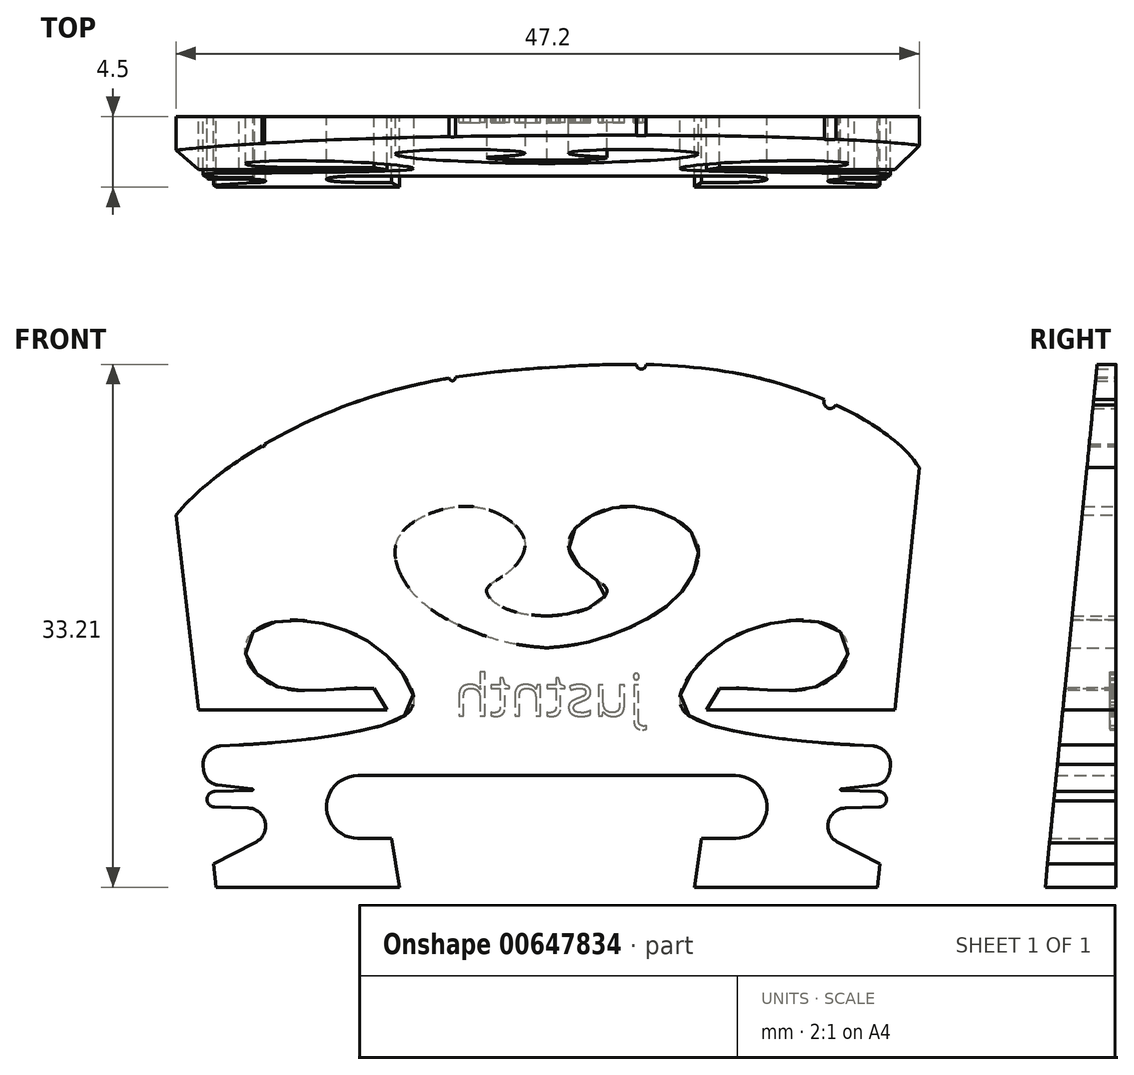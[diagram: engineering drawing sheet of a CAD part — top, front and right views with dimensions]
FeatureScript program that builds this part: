
annotation { "Feature Type Name" : "Feature", "Feature Type Description" : "" }
export const myFeature = defineFeature(function(context is Context, id is Id, definition is map)
    precondition{}
    {
        {
            var Q0;
            Q0=qCreatedBy(makeId("Front.planeOp"),FACE);
            var sketch = newSketch(context, id + "F0", { "sketchPlane" : qUnion([Q0])});
            skFitSpline(sketch, "E0", {"points": [v(-23.54, 23.66) * mm, v(-12.1, 30.83) * mm, v(0, 33) * mm, v(13.95, 32.22) * mm, v(23.66, 26.65) * mm], "startDerivative": vector(29.69, 35.16) * mm, "endDerivative": vector(19.16, -29.67) * mm});
            skLineSegment(sketch, "E1", {"start": v(9.82, 3.09) * mm, "end": v(12, 3.1) * mm});
            skLineSegment(sketch, "E2", {"start": v(12, 7.1) * mm, "end": v(0, 7.1) * mm});
            skArc(sketch, "E3.filletArc", {"start": v(12, 3.1) * mm, "mid": v(14, 5.1) * mm, "end": v(12, 7.1) * mm});
            skLineSegment(sketch, "E4", {"start": v(21, 0) * mm, "end": v(21.16, 1.5) * mm});
            skPoint(sketch, "E5.visualSharp", {"position": v(11.23, 5.08) * mm});
            skFitSpline(sketch, "E6", {"points": [v(0, 15.2) * mm, v(4, 15.99) * mm, v(8.17, 18.33) * mm, v(9.57, 21.81) * mm, v(7.19, 23.82) * mm, v(3.6, 23.93) * mm, v(1.4, 21.97) * mm, v(2.5, 19.96) * mm, v(3.82, 18.86) * mm, v(2.74, 17.76) * mm, v(0, 17.22) * mm], "startDerivative": vector(53.54, 4.7) * mm, "endDerivative": vector(-27.32, -1.62) * mm});
            skFitSpline(sketch, "E7.MirrorCS", {"points": [v(0, 15.2) * mm, v(-4, 15.99) * mm, v(-8.17, 18.33) * mm, v(-9.57, 21.81) * mm, v(-7.19, 23.82) * mm, v(-3.6, 23.93) * mm, v(-1.4, 21.97) * mm, v(-2.5, 19.96) * mm, v(-3.82, 18.86) * mm, v(-2.74, 17.76) * mm, v(0, 17.22) * mm], "startDerivative": vector(-53.54, 4.7) * mm, "endDerivative": vector(27.32, -1.62) * mm});
            skLineSegment(sketch, "E8.MirrorCS", {"start": v(-12, 7.1) * mm, "end": v(0, 7.1) * mm});
            skArc(sketch, "E9.MirrorCS", {"start": v(-12.01, 3.1) * mm, "mid": v(-14, 5.1) * mm, "end": v(-12, 7.1) * mm});
            skLineSegment(sketch, "E10.MirrorCS", {"start": v(-9.85, 3.08) * mm, "end": v(-12.01, 3.1) * mm});
            skLineSegment(sketch, "E11", {"start": v(-21.16, 1.5) * mm, "end": v(-21, 0) * mm});
            skFitSpline(sketch, "E12.MirrorCS", {"points": [v(10.96, 12.63) * mm, v(17.29, 12.8) * mm, v(19.14, 15.37) * mm, v(17, 16.9) * mm, v(12.21, 16.08) * mm, v(9.91, 14.46) * mm, v(8.57, 12.54) * mm, v(9.18, 10.8) * mm, v(19.55, 9.04) * mm], "startDerivative": vector(28.37, 3.52) * mm, "endDerivative": vector(23.7, -0.72) * mm});
            skLineSegment(sketch, "E13.MirrorCS", {"start": v(10.96, 12.63) * mm, "end": v(10.14, 11.25) * mm});
            skLineSegment(sketch, "E14", {"start": v(-18, 62.47) * mm, "end": v(-18, 22.93) * mm, "construction": true});
            skLineSegment(sketch, "E15", {"start": v(6, 60.56) * mm, "end": v(6, 29.37) * mm, "construction": true});
            skLineSegment(sketch, "E16", {"start": v(18, 61.03) * mm, "end": v(18, 25.82) * mm, "construction": true});
            skLineSegment(sketch, "E17", {"start": v(-6, 62.47) * mm, "end": v(-6, 28.49) * mm, "construction": true});
            skCircle(sketch, "E18", {"center": v(-18, 28.08) * mm, "radius": 0.1 * mm});
            skCircle(sketch, "E19", {"center": v(-6, 32.36) * mm, "radius": 0.2 * mm});
            skCircle(sketch, "E20", {"center": v(18, 30.8) * mm, "radius": 0.4 * mm});
            skCircle(sketch, "E21", {"center": v(6, 33.2) * mm, "radius": 0.3 * mm});
            skLineSegment(sketch, "E22", {"start": v(23.66, 26.65) * mm, "end": v(22.12, 11.25) * mm});
            skLineSegment(sketch, "E23", {"start": v(22.12, 11.25) * mm, "end": v(10.14, 11.25) * mm});
            skLineSegment(sketch, "E24", {"start": v(21.16, 1.5) * mm, "end": v(18.56, 2.82) * mm});
            skLineSegment(sketch, "E25", {"start": v(20.7, 8.97) * mm, "end": v(19.55, 9.04) * mm});
            skLineSegment(sketch, "E26", {"start": v(18.96, 5.03) * mm, "end": v(21.1, 5.08) * mm});
            skArc(sketch, "E27", {"start": v(18.96, 5.03) * mm, "mid": v(17.86, 4.1) * mm, "end": v(18.56, 2.82) * mm});
            skPoint(sketch, "E28.visualSharp", {"position": v(21.52, 5.1) * mm});
            skArc(sketch, "E28.filletArc", {"start": v(21.1, 5.08) * mm, "mid": v(21.4, 5.2) * mm, "end": v(21.57, 5.47) * mm});
            skLineSegment(sketch, "E29", {"start": v(21.57, 5.47) * mm, "end": v(21.58, 5.52) * mm});
            skArc(sketch, "E30.filletArc", {"start": v(21.58, 5.52) * mm, "mid": v(21.45, 5.9) * mm, "end": v(21.08, 6.07) * mm});
            skArc(sketch, "E31.filletArc", {"start": v(21.83, 7.8) * mm, "mid": v(21.5, 8.6) * mm, "end": v(20.7, 8.97) * mm});
            skLineSegment(sketch, "E32", {"start": v(21.08, 6.07) * mm, "end": v(18.71, 6.15) * mm});
            skFitSpline(sketch, "E33.MirrorCS", {"points": [v(-10.96, 12.63) * mm, v(-17.29, 12.8) * mm, v(-19.14, 15.37) * mm, v(-17, 16.9) * mm, v(-12.21, 16.08) * mm, v(-9.91, 14.46) * mm, v(-8.57, 12.54) * mm, v(-9.18, 10.8) * mm, v(-19.55, 9.04) * mm], "startDerivative": vector(-28.37, 3.52) * mm, "endDerivative": vector(-23.7, -0.72) * mm});
            skLineSegment(sketch, "E34.MirrorCS", {"start": v(-10.96, 12.63) * mm, "end": v(-10.14, 11.25) * mm});
            skLineSegment(sketch, "E35.MirrorCS", {"start": v(-22.12, 11.25) * mm, "end": v(-10.14, 11.25) * mm});
            skLineSegment(sketch, "E36.MirrorCS", {"start": v(-18.96, 5.03) * mm, "end": v(-21.1, 5.08) * mm});
            skArc(sketch, "E37.MirrorCS", {"start": v(-18.96, 5.03) * mm, "mid": v(-17.86, 4.1) * mm, "end": v(-18.56, 2.82) * mm});
            skLineSegment(sketch, "E38.MirrorCS", {"start": v(-21.16, 1.5) * mm, "end": v(-18.56, 2.82) * mm});
            skLineSegment(sketch, "E39", {"start": v(-22.12, 11.25) * mm, "end": v(-23.54, 23.66) * mm});
            skLineSegment(sketch, "E40", {"start": v(18.7, 6.25) * mm, "end": v(20.9, 6.49) * mm});
            skLineSegment(sketch, "E41", {"start": v(21.78, 7.37) * mm, "end": v(21.83, 7.8) * mm});
            skArc(sketch, "E42.filletArc", {"start": v(20.9, 6.49) * mm, "mid": v(21.5, 6.77) * mm, "end": v(21.78, 7.37) * mm});
            skPoint(sketch, "E43.visualSharp", {"position": v(18, 6.17) * mm});
            skArc(sketch, "E43.filletArc", {"start": v(18.7, 6.25) * mm, "mid": v(18.66, 6.2) * mm, "end": v(18.71, 6.15) * mm});
            skLineSegment(sketch, "E44.MirrorCS", {"start": v(-20.7, 8.97) * mm, "end": v(-19.55, 9.04) * mm});
            skArc(sketch, "E45.MirrorCS", {"start": v(-21.83, 7.8) * mm, "mid": v(-21.5, 8.6) * mm, "end": v(-20.7, 8.97) * mm});
            skLineSegment(sketch, "E46.MirrorCS", {"start": v(-21.78, 7.37) * mm, "end": v(-21.83, 7.8) * mm});
            skArc(sketch, "E47.MirrorCS", {"start": v(-20.9, 6.49) * mm, "mid": v(-21.5, 6.77) * mm, "end": v(-21.78, 7.37) * mm});
            skLineSegment(sketch, "E48.MirrorCS", {"start": v(-18.7, 6.25) * mm, "end": v(-20.9, 6.49) * mm});
            skArc(sketch, "E49.MirrorCS", {"start": v(-18.7, 6.25) * mm, "mid": v(-18.66, 6.2) * mm, "end": v(-18.71, 6.15) * mm});
            skLineSegment(sketch, "E50.MirrorCS", {"start": v(-21.08, 6.07) * mm, "end": v(-18.71, 6.15) * mm});
            skArc(sketch, "E51.MirrorCS", {"start": v(-21.58, 5.52) * mm, "mid": v(-21.45, 5.9) * mm, "end": v(-21.08, 6.07) * mm});
            skArc(sketch, "E52.MirrorCS", {"start": v(-21.1, 5.08) * mm, "mid": v(-21.4, 5.2) * mm, "end": v(-21.57, 5.47) * mm});
            skLineSegment(sketch, "E53.MirrorCS", {"start": v(-21.57, 5.47) * mm, "end": v(-21.58, 5.52) * mm});
            skLineSegment(sketch, "E54", {"start": v(-9.85, 3.08) * mm, "end": v(-9.36, 0) * mm});
            skLineSegment(sketch, "E55", {"start": v(-9.36, 0) * mm, "end": v(-21, 0) * mm});
            skLineSegment(sketch, "E56", {"start": v(9.39, 0) * mm, "end": v(21, 0) * mm});
            skLineSegment(sketch, "E57", {"start": v(9.82, 3.09) * mm, "end": v(9.39, 0) * mm});
            skSolve(sketch);
        }
        {
            var Q0;
            {var subQ1=sQuery(id+"F0.wireOp",EDGE,"E0");Q0=makeQuery(id+"F0.imprint","IMPRINT",FACE,{"disambiguationData":[TD([[makeQuery(id+"F0.imprint","IMPRINT",EDGE,{"derivedFrom":subQ1}),-1.0]])]});}
            extrude(context, id + "F1", {"entities" : qUnion([Q0]), "depth" : 4.5 * mm, "offsetDistance" : 25.4 * mm});
        }
        {
            var Q0;
            Q0=qCreatedBy(makeId("Right.planeOp"),FACE);
            var sketch = newSketch(context, id + "F2", { "sketchPlane" : qUnion([Q0])});
            skLineSegment(sketch, "E58", {"start": v(-1.2, 78.1) * mm, "end": v(-1.2, 1.9) * mm});
            skLineSegment(sketch, "E59", {"start": v(12.46, 33.21) * mm, "end": v(-25.03, 33.21) * mm});
            skLineSegment(sketch, "E60", {"start": v(-4.5, -2.46) * mm, "end": v(-4.5, 45.63) * mm});
            skLineSegment(sketch, "E61", {"start": v(-1.2, 33.21) * mm, "end": v(-4.5, 0) * mm});
            skLineSegment(sketch, "E62", {"start": v(-4.5, 0) * mm, "end": v(-9, 0) * mm});
            skLineSegment(sketch, "E63", {"start": v(-9, 0) * mm, "end": v(-7.85, 33.21) * mm});
            skLineSegment(sketch, "E64", {"start": v(-7.85, 33.21) * mm, "end": v(-1.2, 33.21) * mm});
            skLineSegment(sketch, "E65.top", {"start": v(-7.85, 40.77) * mm, "end": v(-1.2, 40.77) * mm});
            skLineSegment(sketch, "E65.left", {"start": v(-7.85, 33.21) * mm, "end": v(-7.85, 40.77) * mm});
            skLineSegment(sketch, "E65.right", {"start": v(-1.2, 33.21) * mm, "end": v(-1.2, 40.77) * mm});
            skSolve(sketch);
        }
        {
            var Q0;
            {var subQ0=sQuery(id+"F2.wireOp",EDGE,"E62");Q0=makeQuery(id+"F2.imprint","IMPRINT",FACE,{"disambiguationData":[TD([[makeQuery(id+"F2.imprint","IMPRINT",EDGE,{"derivedFrom":subQ0}),-1.0]])]});}
            var Q1;
            {var subQ0=sQuery(id+"F2.wireOp",EDGE,"E61");Q1=makeQuery(id+"F2.imprint","IMPRINT",FACE,{"disambiguationData":[TD([[makeQuery(id+"F2.imprint","IMPRINT",EDGE,{"derivedFrom":subQ0}),-1.0]])]});}
            var Q2;
            {var subQ5=sQuery(id+"F2.wireOp",EDGE,"E65.left");Q2=makeQuery(id+"F2.imprint","IMPRINT",FACE,{"disambiguationData":[TD([[makeQuery(id+"F2.imprint","IMPRINT",EDGE,{"derivedFrom":subQ5}),-1.0]])]});}
            var Q3;
            {var subQ5=sQuery(id+"F2.wireOp",EDGE,"E65.right");Q3=makeQuery(id+"F2.imprint","IMPRINT",FACE,{"disambiguationData":[TD([[makeQuery(id+"F2.imprint","IMPRINT",EDGE,{"derivedFrom":subQ5}),1.0]])]});}
            extrude(context, id + "F3", {"entities" : qUnion([Q0, Q1, Q2, Q3]), "operationType" : NewBodyOperationType.REMOVE, "endBound" : BoundingType.SYMMETRIC, "depth" : 60 * mm, "offsetDistance" : 25.4 * mm});
        }
        {
            var Q0;
            Q0=makeQuery(id+"F1.opExtrude","CAP_FACE",FACE,{"disambiguationData":[OSD([sQuery(id+"F0.wireOp",EDGE,"E0"),sQuery(id+"F0.wireOp",EDGE,"e4hmPngl-bTp4-2FKX-qq5L-C8yQQZpSV2t0"),sQuery(id+"F0.wireOp",EDGE,"m3C9ovOK-315E-PIzk-nrXY-3GBNYPGDzf1G"),sQuery(id+"F0.wireOp",EDGE,"E1"),sQuery(id+"F0.wireOp",EDGE,"E2"),sQuery(id+"F0.wireOp",EDGE,"E3.filletArc"),sQuery(id+"F0.wireOp",EDGE,"E4"),sQuery(id+"F0.wireOp",EDGE,"E6"),sQuery(id+"F0.wireOp",EDGE,"E7.MirrorCS"),sQuery(id+"F0.wireOp",EDGE,"E8.MirrorCS"),sQuery(id+"F0.wireOp",EDGE,"E9.MirrorCS"),sQuery(id+"F0.wireOp",EDGE,"E10.MirrorCS"),sQuery(id+"F0.wireOp",EDGE,"369ba2a7-3018-45a9-8760-523ebc0fda910.MirrorCS"),sQuery(id+"F0.wireOp",EDGE,"99c2ba22-9a41-4c2a-bd8a-ffb563d2db590.MirrorCS"),sQuery(id+"F0.wireOp",EDGE,"E11"),sQuery(id+"F0.wireOp",EDGE,"sNap6CoO-IBVS-i1IY-ntVr-FjdyHk4U1fLk"),sQuery(id+"F0.wireOp",EDGE,"Q49nbHIn-tZww-OQF0-PmV4-upVZ2FfT46EY"),sQuery(id+"F0.wireOp",EDGE,"cacc4af9-22af-473b-8ac6-10344cc65f12.filletArc"),sQuery(id+"F0.wireOp",EDGE,"b2179551-9911-4662-ab98-ed61c98f1fae0.MirrorCS"),sQuery(id+"F0.wireOp",EDGE,"WLDu3wvJ-hjGy-TZ6D-QxCG-5IQINUcYNDWe"),sQuery(id+"F0.wireOp",EDGE,"c432bdc4-3a2f-4fb0-98df-54dfc78423e7.filletArc"),sQuery(id+"F0.wireOp",EDGE,"686801cf-beb7-4a0b-9bdc-b307e84039be.filletArc"),sQuery(id+"F0.wireOp",EDGE,"xwyop2li-xI9W-UFQn-VAwa-afb1EGiimQMJ"),sQuery(id+"F0.wireOp",EDGE,"5a9beed9-85af-4595-b0f8-0b7d7c26e17c"),sQuery(id+"F0.wireOp",EDGE,"bzGZhi7p-2t2n-dACa-pQoM-uhUXtXE2D66O"),sQuery(id+"F0.wireOp",EDGE,"yywPAmDP-Yir0-P9Cb-WB6Q-Zl7V1TjRpGde"),sQuery(id+"F0.wireOp",EDGE,"E12.MirrorCS"),sQuery(id+"F0.wireOp",EDGE,"E13.MirrorCS"),sQuery(id+"F0.wireOp",EDGE,"PqBrF7gv-Diou-TzOB-6hR5-WF0VOCTdd9Ml"),sQuery(id+"F0.wireOp",EDGE,"irIPY5CA-CWUD-HGs8-Lafv-b9PyqiYwdKW4"),sQuery(id+"F0.wireOp",EDGE,"N699qDvk-ju4z-pMcA-En7K-C2CTM2OkSit7"),sQuery(id+"F0.wireOp",EDGE,"uBNGByd7-gyzj-997R-8Wxi-t9WqYOMEbmyB"),sQuery(id+"F0.wireOp",EDGE,"5093e992-0bc9-46ed-b494-589bb84dc8b9.filletArc"),sQuery(id+"F0.wireOp",EDGE,"d6a4b0fc-a71b-4a5d-b080-7cea932b6cd3.filletArc"),sQuery(id+"F0.wireOp",EDGE,"E18"),sQuery(id+"F0.wireOp",EDGE,"E19"),sQuery(id+"F0.wireOp",EDGE,"E20"),sQuery(id+"F0.wireOp",EDGE,"E21"),sQuery(id+"F0.wireOp",EDGE,"zmxQx3sE-Abgh-AzOG-xcvg-COG9eKqwMoW1"),sQuery(id+"F0.wireOp",EDGE,"6rnEQyg1-XuVb-NNO3-yQ0c-2cqNmvtJoFj3"),sQuery(id+"F0.wireOp",EDGE,"a740fce4-74ea-4a46-8614-070f5a65ce19.filletArc"),sQuery(id+"F0.wireOp",EDGE,"47d1662d-1cdc-404f-a2f1-9a71518fff21.filletArc"),sQuery(id+"F0.wireOp",EDGE,"x81WzDIV-gmfL-YwrE-CoO7-FSQeT6FRB7PQ"),sQuery(id+"F0.wireOp",EDGE,"GdfCoyAb-hPPH-aXcI-0p9N-VLlFjwOMujNR"),sQuery(id+"F0.wireOp",EDGE,"af57f127-2944-47e9-8a9b-73b34502bf92.filletArc"),sQuery(id+"F0.wireOp",EDGE,"19e7adce-8ca8-4fdb-b1fc-b8dd92e8bc45.filletArc")])],"isStart":true});
            var sketch = newSketch(context, id + "F4", { "sketchPlane" : qUnion([Q0])});
            skText(sketch, "E66", { "text": "justnth", "fontName": "OpenSans-Regular.ttf"});
            const initialGuessF4  = {"E66": [-0.00615, 0.01088, 1, 0, 0.00264]};
            skSetInitialGuess(sketch, initialGuessF4);
            skSolve(sketch);
        }
        {
            var Q0;
            Q0=qSketchRegion(id+"F4",true);
            extrude(context, id + "F5", {"entities" : qUnion([Q0]), "operationType" : NewBodyOperationType.REMOVE, "oppositeDirection" : true, "depth" : 0.4 * mm, "offsetDistance" : 25.4 * mm});
        }
    });
